# Revit family: Toilet-Elongated-American_Standard-Reliant-250AA.104
name_source: partatom
category: Plumbing Fixtures
units: mm (PartAtom-declared; Revit-internal decimal feet)

## family parameters
Always vertical = No
Cut with Voids When Loaded = No
OmniClass Number = 23.45.05.21.11.11
OmniClass Title = Water Operated Water Closets
Part Type = Normal
Room Calculation Point = No
Round Connector Dimension = Use Radius
Shared = Yes
Work Plane-Based = Yes

## types (1)
- 250AA.104.020
    ADA Compliant = Yes
    Assembly Code = D2010110
    Bowl Shape = Elongated
    CW Connection = Yes
    CWFU = 10
    Cold Water Connection Diameter = 1/2"
    Cold Water Connection Height = 10"
    Cold Water Connection Radius = 1/4"
    Cold Water Connection Width = 6"
    Default Elevation = 0"
    Description = Reliant™ Chair Height Elongated 12" Rough Toilet
    Finish = Vitreous China-American Standard-020-White
    Flush Rate = 1.28 gpf (4.8 Lpf)
    HW Connection = No
    HWFU = 0
    Height = 29 15/16"
    Installation Type = Floor Mounted
    Length = 29 3/4"
    Manufacturer = American Standard
    Material = Vitreous China-American Standard-020-White
    Model = 250AA.104.020
    Price = Prices may vary. Please consult Manufacturer Representative for most up-to-date price list.
    URL = http://www.americanstandard-us.com
    Vent Connection = No
    WFU = 10
    Warranty Information = Limited lifetime warranty on chinaware, limited 2 year warranty on all mechanical parts
and limited 1 year warranty on seat which is
purchased separately
    Waste Connection = Yes
    Waste Connection Diameter = 2"
    Waste Connection Radius = 1"
    Width = 17 15/16"

## geometry (parser evidence)
native form markers: Sweep x3
no freeform markers — native parametric forms only
